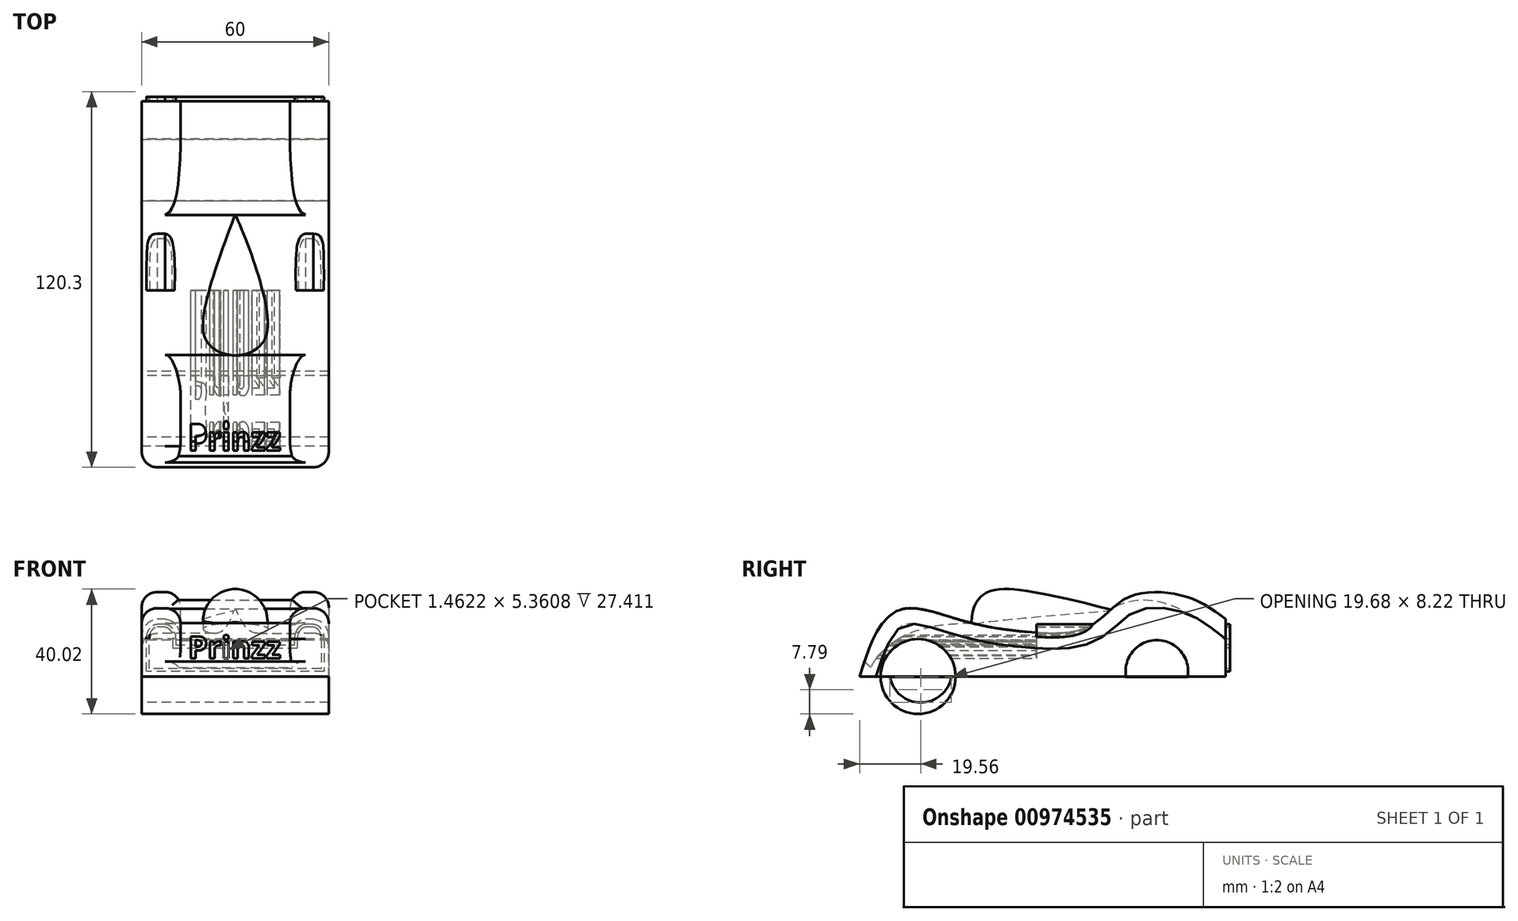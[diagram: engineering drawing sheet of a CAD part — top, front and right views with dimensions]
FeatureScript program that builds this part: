
annotation { "Feature Type Name" : "Feature", "Feature Type Description" : "" }
export const myFeature = defineFeature(function(context is Context, id is Id, definition is map)
    precondition{}
    {
        {
            var Q0;
            Q0=qCreatedBy(makeId("Right.planeOp"),FACE);
            var sketch = newSketch(context, id + "F0", { "sketchPlane" : qUnion([Q0])});
            skCircle(sketch, "E0", {"center": v(-37.9, 0) * mm, "radius": 12 * mm});
            skCircle(sketch, "E1", {"center": v(33.8, 2) * mm, "radius": 12 * mm});
            skLineSegment(sketch, "E2", {"start": v(-56.66, 0) * mm, "end": v(60.63, 0) * mm});
            skLineSegment(sketch, "E3", {"start": v(60.63, 0) * mm, "end": v(60.63, 18.36) * mm});
            skFitSpline(sketch, "E4", {"points": [v(-56.66, 0) * mm, v(-51.7, 13.23) * mm, v(-43.01, 21.6) * mm, v(-23.62, 17.88) * mm, v(-1.28, 14.16) * mm, v(17.18, 16.18) * mm, v(29.6, 25.48) * mm, v(48.68, 25.33) * mm, v(60.63, 18.36) * mm], "startDerivative": vector(36.4, 118.46) * mm, "endDerivative": vector(92.56, -69.94) * mm});
            skSolve(sketch);
        }
        {
            var Q0;
            {var subQ8=sQuery(id+"F0.wireOp",EDGE,"E3");Q0=makeQuery(id+"F0.imprint","IMPRINT",FACE,{"disambiguationData":[TD([[makeQuery(id+"F0.imprint","IMPRINT",EDGE,{"derivedFrom":subQ8}),1.0]])]});}
            var Q1;
            {var subQ0=sQuery(id+"F0.wireOp",EDGE,"E2");var subQ1=sQuery(id+"F0.wireOp",EDGE,"E0");var subQ2=makeQuery(id+"F0.imprint","INTERSECT",VERTEX,{"disambiguationData":[OD(0.0)],"derivedFrom":[subQ1,subQ0]});Q1=makeQuery(id+"F0.imprint","IMPRINT",FACE,{"disambiguationData":[TD([[makeQuery(id+"F0.imprint","IMPRINT",EDGE,{"disambiguationData":[TD([[subQ2,1.0]])],"derivedFrom":subQ1}),1.0]])]});}
            var Q2;
            {var subQ0=sQuery(id+"F0.wireOp",EDGE,"E2");var subQ1=sQuery(id+"F0.wireOp",EDGE,"E1");var subQ2=makeQuery(id+"F0.imprint","INTERSECT",VERTEX,{"disambiguationData":[OD(0.0)],"derivedFrom":[subQ1,subQ0]});Q2=makeQuery(id+"F0.imprint","IMPRINT",FACE,{"disambiguationData":[TD([[makeQuery(id+"F0.imprint","IMPRINT",EDGE,{"disambiguationData":[TD([[subQ2,1.0]])],"derivedFrom":subQ1}),1.0]])]});}
            extrude(context, id + "F1", {"entities" : qUnion([Q0, Q1, Q2]), "depth" : 60 * mm, "offsetDistance" : 25 * mm, "symmetric" : true});
        }
        {
            var Q0;
            Q0=qCreatedBy(makeId("Right.planeOp"),FACE);
            var sketch = newSketch(context, id + "F2", { "sketchPlane" : qUnion([Q0])});
            skFitSpline(sketch, "E5", {"points": [v(-20.83, 16.6) * mm, v(-16.96, 26.3) * mm, v(-2.5, 27.33) * mm, v(24.43, 21.24) * mm], "startDerivative": vector(-2.04, 45.75) * mm, "endDerivative": vector(65.9, -17.26) * mm});
            skLineSegment(sketch, "E6", {"start": v(-20.83, 16.6) * mm, "end": v(24.43, 21.24) * mm});
            skSolve(sketch);
        }
        {
            var Q0;
            Q0 = qSketchRegion(id + "F2", true);
            var Q1;
            Q1=sQuery(id+"F2.wireOp",EDGE,"E6");
            revolve(context, id + "F3", {"operationType" : NewBodyOperationType.ADD, "surfaceOperationType" : NewSurfaceOperationType.NEW, "entities" : qUnion([Q0]), "axis" : qUnion([Q1]), "revolveType" : RevolveType.SYMMETRIC, "angle" : 175 * degree});
        }
        {
            var Q0;
            Q0=makeQuery(id+"F3.opRevolve","CAP_FACE",FACE,{"disambiguationData":[OSD([sQuery(id+"F2.wireOp",EDGE,"E5"),sQuery(id+"F2.wireOp",EDGE,"E6")])],"isStart":false});
            var Q1;
            Q1=makeQuery(id+"F3.opRevolve","CAP_FACE",FACE,{"disambiguationData":[OSD([sQuery(id+"F2.wireOp",EDGE,"E5"),sQuery(id+"F2.wireOp",EDGE,"E6")])],"isStart":true});
            extrude(context, id + "F4", {"entities" : qUnion([Q0, Q1]), "operationType" : NewBodyOperationType.ADD, "depth" : 10 * mm, "offsetDistance" : 25 * mm});
        }
        {
            var Q0;
            Q0=qCreatedBy(makeId("Right.planeOp"),FACE);
            var sketch = newSketch(context, id + "F5", { "sketchPlane" : qUnion([Q0])});
            skLineSegment(sketch, "E7", {"start": v(-53.11, 2.97) * mm, "end": v(-71.53, 19.97) * mm});
            skLineSegment(sketch, "E8", {"start": v(-71.53, 19.97) * mm, "end": v(-28.19, 30.45) * mm});
            skLineSegment(sketch, "E9", {"start": v(-28.19, 30.45) * mm, "end": v(-20.65, 17.07) * mm});
            skFitSpline(sketch, "E10", {"points": [v(-53.11, 2.97) * mm, v(-49.34, 8.01) * mm, v(-40.86, 13.78) * mm, v(-20.65, 17.07) * mm], "startDerivative": vector(11.13, 20.79) * mm, "endDerivative": vector(63.9, 2.04) * mm});
            skLineSegment(sketch, "E11", {"start": v(23.81, 21.53) * mm, "end": v(25.89, 35.25) * mm});
            skLineSegment(sketch, "E12", {"start": v(25.89, 35.25) * mm, "end": v(68.13, 28.86) * mm});
            skLineSegment(sketch, "E13", {"start": v(68.13, 28.86) * mm, "end": v(60.59, 11.59) * mm});
            skFitSpline(sketch, "E14", {"points": [v(60.59, 11.59) * mm, v(49.28, 19.92) * mm, v(23.81, 21.53) * mm], "startDerivative": vector(-22.7, 23.23) * mm, "endDerivative": vector(-49.16, -29.67) * mm});
            skSolve(sketch);
        }
        {
            var Q0;
            Q0 = qSketchRegion(id + "F5", true);
            extrude(context, id + "F6", {"entities" : qUnion([Q0]), "operationType" : NewBodyOperationType.REMOVE, "oppositeDirection" : true, "depth" : 35 * mm, "offsetDistance" : 25 * mm, "symmetric" : true});
        }
        {
            var Q0;
            Q0=makeQuery(id+"F6.boolean.opBoolean","INTERSECT",EDGE,{"derivedFrom":[makeQuery(id+"F1.opExtrude","SWEPT_FACE",FACE,{"disambiguationData":[OSD([sQuery(id+"F0.wireOp",EDGE,"E4")])]}),makeQuery(id+"F6.opExtrude","CAP_FACE",FACE,{"disambiguationData":[OSD([sQuery(id+"F5.wireOp",EDGE,"E7"),sQuery(id+"F5.wireOp",EDGE,"E8"),sQuery(id+"F5.wireOp",EDGE,"E9"),sQuery(id+"F5.wireOp",EDGE,"E10")])],"isStart":false})]});
            var Q1;
            Q1=makeQuery(id+"F6.boolean.opBoolean","INTERSECT",EDGE,{"derivedFrom":[makeQuery(id+"F1.opExtrude","SWEPT_FACE",FACE,{"disambiguationData":[OSD([sQuery(id+"F0.wireOp",EDGE,"E4")])]}),makeQuery(id+"F6.opExtrude","CAP_FACE",FACE,{"disambiguationData":[OSD([sQuery(id+"F5.wireOp",EDGE,"E7"),sQuery(id+"F5.wireOp",EDGE,"E8"),sQuery(id+"F5.wireOp",EDGE,"E9"),sQuery(id+"F5.wireOp",EDGE,"E10")])],"isStart":true})]});
            var Q2;
            Q2=makeQuery(id+"F6.boolean.opBoolean","INTERSECT",EDGE,{"derivedFrom":[makeQuery(id+"F1.opExtrude","SWEPT_FACE",FACE,{"disambiguationData":[OSD([sQuery(id+"F0.wireOp",EDGE,"E4")])]}),makeQuery(id+"F6.opExtrude","CAP_FACE",FACE,{"disambiguationData":[OSD([sQuery(id+"F5.wireOp",EDGE,"E11"),sQuery(id+"F5.wireOp",EDGE,"E12"),sQuery(id+"F5.wireOp",EDGE,"E13"),sQuery(id+"F5.wireOp",EDGE,"E14")])],"isStart":false})]});
            var Q3;
            Q3=makeQuery(id+"F6.boolean.opBoolean","INTERSECT",EDGE,{"derivedFrom":[makeQuery(id+"F1.opExtrude","SWEPT_FACE",FACE,{"disambiguationData":[OSD([sQuery(id+"F0.wireOp",EDGE,"E4")])]}),makeQuery(id+"F6.opExtrude","CAP_FACE",FACE,{"disambiguationData":[OSD([sQuery(id+"F5.wireOp",EDGE,"E11"),sQuery(id+"F5.wireOp",EDGE,"E12"),sQuery(id+"F5.wireOp",EDGE,"E13"),sQuery(id+"F5.wireOp",EDGE,"E14")])],"isStart":true})]});
            var Q4;
            Q4=makeQuery(id+"F1.opExtrude","CAP_EDGE",EDGE,{"disambiguationData":[OSD([sQuery(id+"F0.wireOp",EDGE,"E4")])],"isStart":false});
            var Q5;
            Q5=makeQuery(id+"F1.opExtrude","CAP_EDGE",EDGE,{"disambiguationData":[OSD([sQuery(id+"F0.wireOp",EDGE,"E4")])],"isStart":true});
            fillet(context, id + "F7", {"entities" : qUnion([Q0, Q1, Q2, Q3, Q4, Q5]), "radius" : 5 * mm, "tangentPropagation" : true, "allowEdgeOverflow" : false});
        }
        {
            var Q0;
            Q0=qCreatedBy(makeId("Front.planeOp"),FACE);
            var sketch = newSketch(context, id + "F8", { "sketchPlane" : qUnion([Q0])});
            skFitSpline(sketch, "E15.0", {"points": [v(-28.4, 12.1) * mm, v(-28.4, 12.4) * mm, v(-28.36, 12.98) * mm, v(-28.2, 13.68) * mm, v(-28.02, 14.23) * mm, v(-27.8, 14.76) * mm, v(-27.52, 15.23) * mm, v(-27.18, 15.66) * mm, v(-26.91, 15.94) * mm, v(-26.62, 16.19) * mm, v(-26.2, 16.47) * mm, v(-25.78, 16.65) * mm, v(-25.33, 16.75) * mm, v(-25.11, 16.76) * mm, v(-25, 16.76) * mm]});
            skLineSegment(sketch, "E15.1", {"start": v(19.1, 10.09) * mm, "end": v(19.1, 12.1) * mm});
            skLineSegment(sketch, "E15.2", {"start": v(-19.1, 10.09) * mm, "end": v(19.1, 10.09) * mm});
            skLineSegment(sketch, "E15.3", {"start": v(-19.1, 12.1) * mm, "end": v(-19.1, 10.09) * mm});
            skFitSpline(sketch, "E15.4", {"points": [v(-22.5, 16.76) * mm, v(-22.39, 16.76) * mm, v(-22.17, 16.74) * mm, v(-21.84, 16.68) * mm, v(-21.5, 16.56) * mm, v(-21.2, 16.4) * mm, v(-20.89, 16.2) * mm, v(-20.6, 15.95) * mm, v(-20.32, 15.67) * mm, v(-20.07, 15.35) * mm, v(-19.85, 15) * mm, v(-19.65, 14.63) * mm, v(-19.48, 14.24) * mm, v(-19.3, 13.69) * mm, v(-19.14, 12.98) * mm, v(-19.1, 12.39) * mm, v(-19.1, 12.1) * mm]});
            skFitSpline(sketch, "E15.5", {"points": [v(19.1, 12.1) * mm, v(19.1, 12.4) * mm, v(19.14, 12.98) * mm, v(19.3, 13.68) * mm, v(19.48, 14.23) * mm, v(19.7, 14.76) * mm, v(19.98, 15.23) * mm, v(20.32, 15.66) * mm, v(20.59, 15.94) * mm, v(20.88, 16.19) * mm, v(21.3, 16.47) * mm, v(21.72, 16.65) * mm, v(22.17, 16.75) * mm, v(22.39, 16.76) * mm, v(22.5, 16.76) * mm]});
            skLineSegment(sketch, "E15.6", {"start": v(-25, 16.76) * mm, "end": v(-22.5, 16.76) * mm});
            skLineSegment(sketch, "E15.7", {"start": v(22.5, 16.76) * mm, "end": v(25, 16.76) * mm});
            skFitSpline(sketch, "E15.8", {"points": [v(25, 16.76) * mm, v(25.11, 16.76) * mm, v(25.33, 16.74) * mm, v(25.66, 16.68) * mm, v(26, 16.56) * mm, v(26.3, 16.4) * mm, v(26.61, 16.2) * mm, v(26.9, 15.95) * mm, v(27.18, 15.67) * mm, v(27.43, 15.35) * mm, v(27.65, 15) * mm, v(27.85, 14.63) * mm, v(28.02, 14.24) * mm, v(28.2, 13.69) * mm, v(28.36, 12.98) * mm, v(28.4, 12.39) * mm, v(28.4, 12.1) * mm]});
            skLineSegment(sketch, "E15.9", {"start": v(28.4, 12.1) * mm, "end": v(28.4, 1.6) * mm});
            skLineSegment(sketch, "E15.10", {"start": v(28.4, 1.6) * mm, "end": v(-28.4, 1.6) * mm});
            skLineSegment(sketch, "E15.11", {"start": v(-28.4, 1.6) * mm, "end": v(-28.4, 12.1) * mm});
            skFitSpline(sketch, "E16.0", {"points": [v(-27.5, 12.1) * mm, v(-27.5, 12.35) * mm, v(-27.46, 12.85) * mm, v(-27.33, 13.45) * mm, v(-27.18, 13.91) * mm, v(-27.04, 14.24) * mm, v(-26.88, 14.54) * mm, v(-26.7, 14.82) * mm, v(-26.5, 15.07) * mm, v(-26.3, 15.29) * mm, v(-26.08, 15.47) * mm, v(-25.78, 15.67) * mm, v(-25.5, 15.79) * mm, v(-25.2, 15.85) * mm, v(-25.07, 15.86) * mm, v(-25, 15.86) * mm]});
            skLineSegment(sketch, "E16.1", {"start": v(20, 9.19) * mm, "end": v(20, 12.1) * mm});
            skLineSegment(sketch, "E16.2", {"start": v(-20, 9.19) * mm, "end": v(20, 9.19) * mm});
            skLineSegment(sketch, "E16.3", {"start": v(-20, 12.1) * mm, "end": v(-20, 9.19) * mm});
            skFitSpline(sketch, "E16.4", {"points": [v(-22.5, 15.86) * mm, v(-22.43, 15.86) * mm, v(-22.3, 15.85) * mm, v(-22.09, 15.8) * mm, v(-21.9, 15.74) * mm, v(-21.76, 15.68) * mm, v(-21.65, 15.62) * mm, v(-21.54, 15.55) * mm, v(-21.4, 15.44) * mm, v(-21.2, 15.29) * mm, v(-21, 15.08) * mm, v(-20.8, 14.82) * mm, v(-20.62, 14.54) * mm, v(-20.46, 14.24) * mm, v(-20.32, 13.92) * mm, v(-20.17, 13.45) * mm, v(-20.04, 12.86) * mm, v(-20, 12.35) * mm, v(-20, 12.1) * mm]});
            skFitSpline(sketch, "E16.5", {"points": [v(20, 12.1) * mm, v(20, 12.35) * mm, v(20.04, 12.85) * mm, v(20.17, 13.45) * mm, v(20.32, 13.91) * mm, v(20.46, 14.24) * mm, v(20.62, 14.54) * mm, v(20.8, 14.82) * mm, v(21, 15.07) * mm, v(21.2, 15.29) * mm, v(21.42, 15.47) * mm, v(21.72, 15.67) * mm, v(22, 15.79) * mm, v(22.3, 15.85) * mm, v(22.43, 15.86) * mm, v(22.5, 15.86) * mm]});
            skLineSegment(sketch, "E16.6", {"start": v(-25, 15.86) * mm, "end": v(-22.5, 15.86) * mm});
            skLineSegment(sketch, "E16.7", {"start": v(22.5, 15.86) * mm, "end": v(25, 15.86) * mm});
            skFitSpline(sketch, "E16.8", {"points": [v(25, 15.86) * mm, v(25.07, 15.86) * mm, v(25.2, 15.85) * mm, v(25.41, 15.8) * mm, v(25.6, 15.74) * mm, v(25.74, 15.68) * mm, v(25.85, 15.62) * mm, v(25.96, 15.55) * mm, v(26.1, 15.44) * mm, v(26.3, 15.29) * mm, v(26.5, 15.08) * mm, v(26.7, 14.82) * mm, v(26.88, 14.54) * mm, v(27.04, 14.24) * mm, v(27.18, 13.92) * mm, v(27.33, 13.45) * mm, v(27.46, 12.86) * mm, v(27.5, 12.35) * mm, v(27.5, 12.1) * mm]});
            skLineSegment(sketch, "E16.9", {"start": v(27.5, 12.1) * mm, "end": v(27.5, 2.5) * mm});
            skLineSegment(sketch, "E16.10", {"start": v(27.5, 2.5) * mm, "end": v(-27.5, 2.5) * mm});
            skLineSegment(sketch, "E16.11", {"start": v(-27.5, 2.5) * mm, "end": v(-27.5, 12.1) * mm});
            skSolve(sketch);
        }
        {
            var Q0;
            Q0 = qSketchRegion(id + "F8", true);
            extrude(context, id + "F9", {"entities" : qUnion([Q0]), "operationType" : NewBodyOperationType.ADD, "oppositeDirection" : true, "depth" : 62 * mm, "offsetDistance" : 25 * mm});
        }
        {
            var Q0;
            Q0=qCreatedBy(makeId("Right.planeOp"),FACE);
            var sketch = newSketch(context, id + "F10", { "sketchPlane" : qUnion([Q0])});
            skCircle(sketch, "E17", {"center": v(-37.1, 1.68) * mm, "radius": 10 * mm});
            skCircle(sketch, "E18", {"center": v(38.55, 1.68) * mm, "radius": 10 * mm});
            skSolve(sketch);
        }
        {
            var Q0;
            Q0 = qSketchRegion(id + "F10", true);
            extrude(context, id + "F11", {"entities" : qUnion([Q0]), "operationType" : NewBodyOperationType.REMOVE, "depth" : 77 * mm, "offsetDistance" : 25 * mm});
        }
        {
            var Q0;
            Q0 = qSketchRegion(id + "F10", true);
            extrude(context, id + "F12", {"entities" : qUnion([Q0]), "operationType" : NewBodyOperationType.REMOVE, "oppositeDirection" : true, "depth" : 85 * mm, "offsetDistance" : 25 * mm});
        }
        {
            var Q0;
            Q0=qCreatedBy(makeId("Front.planeOp"),FACE);
            var sketch = newSketch(context, id + "F13", { "sketchPlane" : qUnion([Q0])});
            skText(sketch, "E19", { "text": "Prinzz", "fontName": "OpenSans-Bold.ttf"});
            const initialGuessF13  = {"E19": [-0.01504, 0.00583, 1, 0, 0.00707]};
            skSetInitialGuess(sketch, initialGuessF13);
            skSolve(sketch);
        }
        {
            var Q0;
            Q0 = qSketchRegion(id + "F13", true);
            extrude(context, id + "F14", {"entities" : qUnion([Q0]), "operationType" : NewBodyOperationType.REMOVE, "depth" : 59.2 * mm, "offsetDistance" : 25 * mm});
        }
        {
            var Q0;
            Q0=qCreatedBy(makeId("Top.planeOp"),FACE);
            var sketch = newSketch(context, id + "F15", { "sketchPlane" : qUnion([Q0])});
            skLineSegment(sketch, "E20.bottom", {"start": v(-30, -46.98) * mm, "end": v(30, -46.98) * mm});
            skLineSegment(sketch, "E20.top", {"start": v(-30, -27.24) * mm, "end": v(30, -27.24) * mm});
            skLineSegment(sketch, "E20.left", {"start": v(-30, -46.98) * mm, "end": v(-30, -27.24) * mm});
            skLineSegment(sketch, "E20.right", {"start": v(30, -46.98) * mm, "end": v(30, -27.24) * mm});
            skSolve(sketch);
        }
        {
            var Q0;
            Q0=makeQuery(id+"F15.imprint","IMPRINT",FACE,{"disambiguationData":[TD([[makeQuery(id+"F15.imprint","IMPRINT",EDGE,{"derivedFrom":sQuery(id+"F15.wireOp",EDGE,"E20.bottom")}),1.0]])]});
            extrude(context, id + "F16", {"entities" : qUnion([Q0]), "operationType" : NewBodyOperationType.ADD, "oppositeDirection" : true, "depth" : 0.1 * mm, "offsetDistance" : 25 * mm});
        }
        {
            var Q0;
            Q0=qCreatedBy(makeId("Top.planeOp"),FACE);
            var sketch = newSketch(context, id + "F17", { "sketchPlane" : qUnion([Q0])});
            skLineSegment(sketch, "E21.bottom", {"start": v(-30, 28.65) * mm, "end": v(29.99, 28.65) * mm});
            skLineSegment(sketch, "E21.top", {"start": v(-30, 48.42) * mm, "end": v(29.99, 48.42) * mm});
            skLineSegment(sketch, "E21.left", {"start": v(-30, 28.65) * mm, "end": v(-30, 48.42) * mm});
            skLineSegment(sketch, "E21.right", {"start": v(29.99, 28.65) * mm, "end": v(29.99, 48.42) * mm});
            skSolve(sketch);
        }
        {
            var Q0;
            Q0 = qSketchRegion(id + "F17", true);
            extrude(context, id + "F18", {"entities" : qUnion([Q0]), "operationType" : NewBodyOperationType.ADD, "oppositeDirection" : true, "depth" : 0.1 * mm, "offsetDistance" : 25 * mm});
        }
        {
            var Q0;
            Q0=makeQuery(id+"F14.boolean.opBoolean","SPLIT",BODY,{"disambiguationData":[OD(0.0)],"derivedFrom":makeQuery(id+"F1.opExtrude","SWEPT_BODY",BODY,{"disambiguationData":[OSD([sQuery(id+"F0.wireOp",EDGE,"E2"),sQuery(id+"F0.wireOp",EDGE,"E3"),sQuery(id+"F0.wireOp",EDGE,"E4")])]})});
            deleteBodies(context, id + "F19", {"entities" : qUnion([Q0])});
        }
    });
